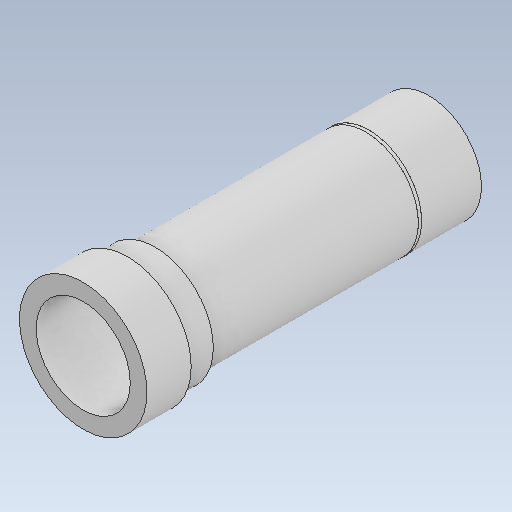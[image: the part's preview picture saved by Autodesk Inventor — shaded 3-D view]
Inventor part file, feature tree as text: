
AUTODESK INVENTOR PART (.ipt)
format: ipt  version: 2021 (Build 250183000, 183)  size: 421,376 bytes
history: native  units: mm
features: extrude x9, sketch x7, plane x2, fillet x1, pattern_circular x1
ambient origin geometry x8: Origin, YZ Plane, XZ Plane, XY Plane, X Axis, Y Axis, Z Axis, Center Point
bodies: Solid1 (feature_tree)
feature tree (20):
  sketch  "Sketch1"  dims[d0=90.0mm]
  extrude  "Extrusion2"  Depth=10.0mm TaperAngle=0.0deg
  fillet  "Fillet1"  Radius=3.0mm
  extrude  "Extrusion3"  Depth=360.0mm TaperAngle=360.0deg
  pattern_circular  "Circular Pattern1"  Count=9  [1 undecoded]
  extrude  "Extrusion9"  Depth=29.94mm TaperAngle=0.0deg
  extrude  "Extrusion10"  Depth=3.0mm
  plane  "Work Plane5"
  plane  "Work Plane6"
  sketch  "Sketch11"  dims[d17=0.0mm d18=0.0mm d19=360.0mm d20=360.0deg]
  extrude  "Extrusion14"  Depth=3.0mm
  extrude  "Extrusion16"  Depth=190.0mm TaperAngle=0.0deg
  extrude  "Extrusion17"  Depth=3.0mm
  extrude  "Extrusion19"  Depth=3.0mm
  extrude  "Extrusion20"  Depth=25.0mm TaperAngle=0.0deg
  sketch  "Sketch7"  dims[d1=80.0mm d2=0.0mm d3=0.0mm d4=0.0mm d5=0.0mm d6=74.0mm d7=14.3117mm d8=36.936003mm d9=2.175251mm d10=2.061732mm d11=11.285177mm d14=10.0mm d15=0.0mm d16=3.0mm]
  sketch  "Sketch15"  dims[d49=10.0mm d50=0.0mm d51=90.0mm]
  sketch  "Sketch16"  dims[d52=85.0mm d53=29.94mm d54=0.0mm]
  sketch  "Sketch18"  dims[d55=3.0mm d67=3.0mm]
  sketch  "Sketch19"  dims[d68=95.0mm d69=85.0mm d72=190.0mm d73=0.0mm d78=85.0mm d79=105.0mm d80=25.0mm d81=0.0mm d82=85.0mm d83=115.0mm d84=40.0mm d85=0.0mm d86=90.0mm d87=95.0mm d90=57.07mm d91=0.0mm d92=3.0mm d93=0.0mm d94=0.5mm d95=0.872665mm]
note: 1 required parameter value undecoded (feature->parameter linkage not recoverable at this tier; creation-order binding heuristic only, values carry confidence <= 0.55)
